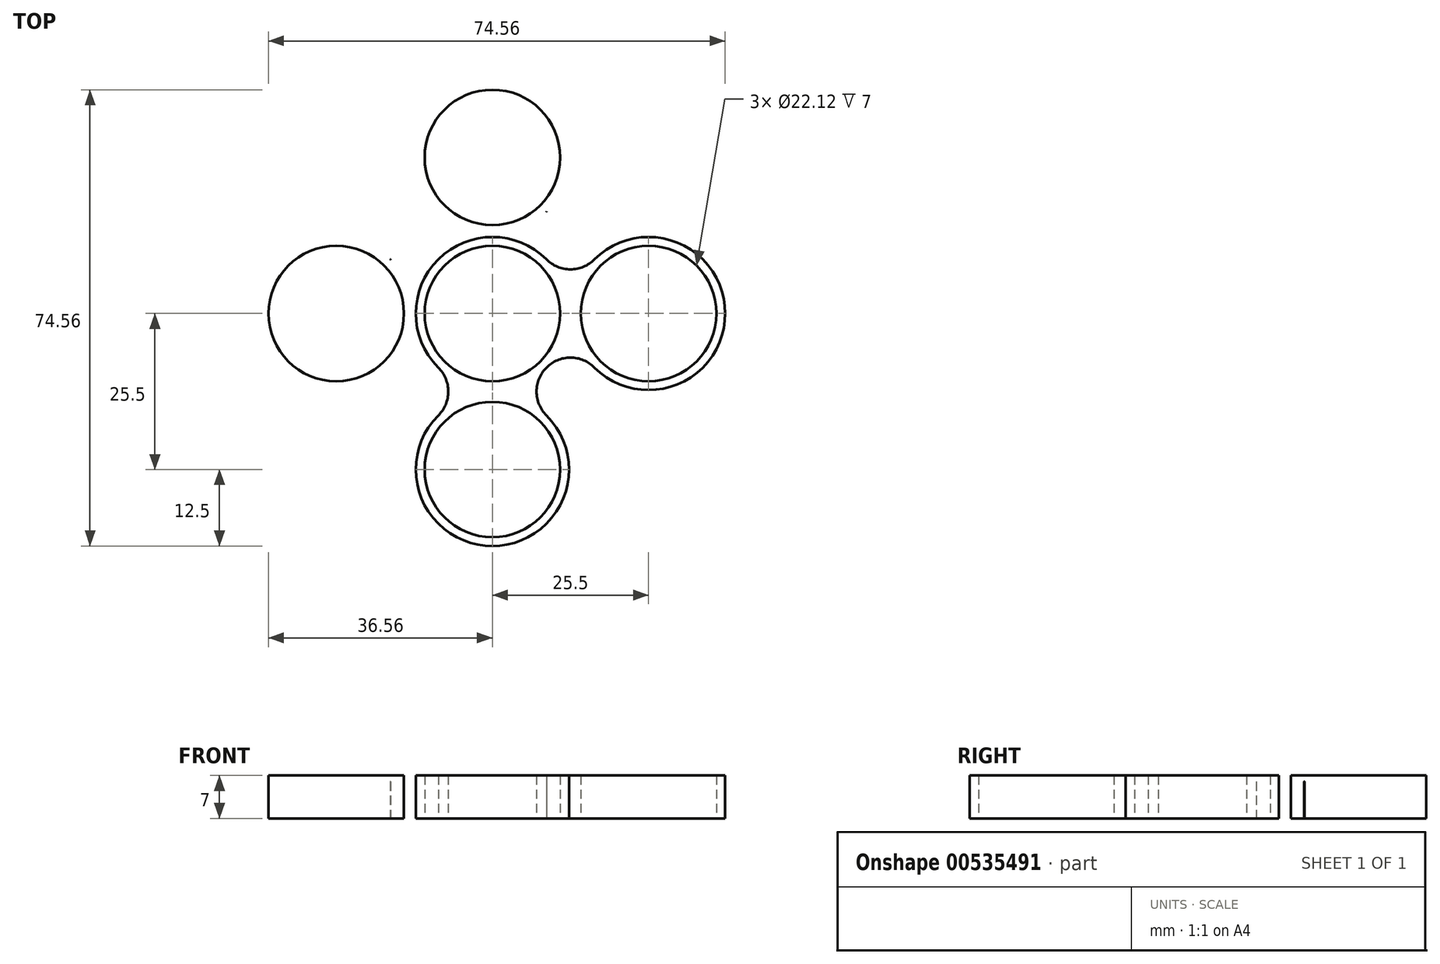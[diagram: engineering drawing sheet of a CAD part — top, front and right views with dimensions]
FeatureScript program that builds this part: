
annotation { "Feature Type Name" : "Feature", "Feature Type Description" : "" }
export const myFeature = defineFeature(function(context is Context, id is Id, definition is map)
    precondition{}
    {
        {
            var Q0;
            Q0=qCreatedBy(makeId("Top.planeOp"),FACE);
            var sketch = newSketch(context, id + "F0", { "sketchPlane" : qUnion([Q0])});
            skCircle(sketch, "E0", {"center": v(0, 0) * mm, "radius": 11.06 * mm});
            skCircle(sketch, "E1", {"center": v(0, 0) * mm, "radius": 12.5 * mm});
            skLineSegment(sketch, "E2", {"start": v(0, 0) * mm, "end": v(11.05, 11.05) * mm, "construction": true});
            skLineSegment(sketch, "E3", {"start": v(11.06, 0) * mm, "end": v(12.5, 0) * mm, "construction": true});
            skLineSegment(sketch, "E4", {"start": v(12.5, 0) * mm, "end": v(25.5, 0) * mm, "construction": true});
            skCircle(sketch, "E5", {"center": v(25.5, 0) * mm, "radius": 11.06 * mm});
            skCircle(sketch, "E6", {"center": v(25.5, 0) * mm, "radius": 12.5 * mm});
            skArc(sketch, "E7", {"start": v(8.84, 8.84) * mm, "mid": v(12.75, 7.2) * mm, "end": v(16.66, 8.84) * mm});
            skArc(sketch, "E8.MirrorCS", {"start": v(8.84, -8.84) * mm, "mid": v(12.75, -7.2) * mm, "end": v(16.66, -8.84) * mm});
            skCircle(sketch, "E9.MirrorC", {"center": v(0, 25.5) * mm, "radius": 12.5 * mm});
            skCircle(sketch, "E10.MirrorC", {"center": v(0, 25.5) * mm, "radius": 11.06 * mm});
            skArc(sketch, "E11.MirrorCS", {"start": v(8.84, 8.84) * mm, "mid": v(7.2, 12.75) * mm, "end": v(8.84, 16.66) * mm});
            skArc(sketch, "E12.MirrorCS", {"start": v(-8.84, 8.84) * mm, "mid": v(-7.2, 12.75) * mm, "end": v(-8.84, 16.66) * mm});
            skCircle(sketch, "E13.MirrorC", {"center": v(-25.5, 0) * mm, "radius": 11.06 * mm});
            skCircle(sketch, "E14.MirrorC", {"center": v(-25.5, 0) * mm, "radius": 12.5 * mm});
            skArc(sketch, "E15.MirrorCS", {"start": v(-8.84, 8.84) * mm, "mid": v(-12.75, 7.2) * mm, "end": v(-16.66, 8.84) * mm});
            skArc(sketch, "E16.MirrorCS", {"start": v(-8.84, -8.84) * mm, "mid": v(-12.75, -7.2) * mm, "end": v(-16.66, -8.84) * mm});
            skCircle(sketch, "E17.MirrorC", {"center": v(0, -25.5) * mm, "radius": 12.5 * mm});
            skCircle(sketch, "E18.MirrorC", {"center": v(0, -25.5) * mm, "radius": 11.06 * mm});
            skArc(sketch, "E19.MirrorCS", {"start": v(8.84, -8.84) * mm, "mid": v(7.2, -12.75) * mm, "end": v(8.84, -16.66) * mm});
            skArc(sketch, "E20.MirrorCS", {"start": v(-8.84, -8.84) * mm, "mid": v(-7.2, -12.75) * mm, "end": v(-8.84, -16.66) * mm});
            skSolve(sketch);
        }
        {
            var Q0;
            Q0=makeQuery(id+"F0.imprint","IMPRINT",FACE,{"disambiguationData":[TD([[makeQuery(id+"F0.imprint","IMPRINT",EDGE,{"derivedFrom":sQuery(id+"F0.wireOp",EDGE,"E0")}),-1.0]])]});
            var Q1;
            {var subQ0=sQuery(id+"F0.wireOp",EDGE,"uPQ4puG7-UEyB-lj3g-LrHJ-iqQRtvX8gU40");Q1=makeQuery(id+"F0.imprint","IMPRINT",FACE,{"disambiguationData":[TD([[makeQuery(id+"F0.imprint","IMPRINT",EDGE,{"derivedFrom":subQ0}),-1.0]])]});}
            var Q2;
            {var subQ0=sQuery(id+"F0.wireOp",EDGE,"09f7ae70-37af-4967-ad5b-0058ab8db1040.MirrorCS");Q2=makeQuery(id+"F0.imprint","IMPRINT",FACE,{"disambiguationData":[TD([[makeQuery(id+"F0.imprint","IMPRINT",EDGE,{"derivedFrom":subQ0}),1.0]])]});}
            var Q3;
            Q3=makeQuery(id+"F0.imprint","IMPRINT",FACE,{"disambiguationData":[TD([[makeQuery(id+"F0.imprint","IMPRINT",EDGE,{"derivedFrom":sQuery(id+"F0.wireOp",EDGE,"MIKsI08s-PwHs-qc6J-BAKb-bbBWn8hbvVMQ")}),1.0]])]});
            var Q4;
            Q4=makeQuery(id+"F0.imprint","IMPRINT",FACE,{"disambiguationData":[TD([[makeQuery(id+"F0.imprint","IMPRINT",EDGE,{"derivedFrom":sQuery(id+"F0.wireOp",EDGE,"MIKsI08s-PwHs-qc6J-BAKb-bbBWn8hbvVMQ")}),-1.0]])]});
            var Q5;
            {var subQ0=sQuery(id+"F0.wireOp",EDGE,"butBKBYa-hvjT-XOIa-KBhH-1ktqhelA6FoJ");var subQ1=sQuery(id+"F0.wireOp",EDGE,"E1");var subQ2=makeQuery(id+"F0.imprint","INTERSECT",VERTEX,{"disambiguationData":[OD(0.0)],"derivedFrom":[subQ1,subQ0]});Q5=makeQuery(id+"F0.imprint","IMPRINT",FACE,{"disambiguationData":[TD([[makeQuery(id+"F0.imprint","IMPRINT",EDGE,{"disambiguationData":[TD([[subQ2,1.0]])],"derivedFrom":subQ1}),1.0]])]});}
            var Q6;
            Q6=makeQuery(id+"F0.imprint","IMPRINT",FACE,{"disambiguationData":[TD([[makeQuery(id+"F0.imprint","IMPRINT",EDGE,{"derivedFrom":sQuery(id+"F0.wireOp",EDGE,"ioFQfvYo-xZlu-Zo4V-6zG4-lo5VrKWCEeY0")}),1.0]])]});
            var Q7;
            Q7=makeQuery(id+"F0.imprint","IMPRINT",FACE,{"disambiguationData":[TD([[makeQuery(id+"F0.imprint","IMPRINT",EDGE,{"derivedFrom":sQuery(id+"F0.wireOp",EDGE,"Zf5WaJAE-leRk-cjoL-8J3G-R3mTZz96XQRM")}),-1.0]])]});
            var Q8;
            {var subQ0=sQuery(id+"F0.wireOp",EDGE,"a43479c8-e354-4f77-97ad-e8487c43b59b0.MirrorCS");Q8=makeQuery(id+"F0.imprint","IMPRINT",FACE,{"disambiguationData":[TD([[makeQuery(id+"F0.imprint","IMPRINT",EDGE,{"derivedFrom":subQ0}),1.0]])]});}
            var Q9;
            Q9=makeQuery(id+"F0.imprint","IMPRINT",FACE,{"disambiguationData":[TD([[makeQuery(id+"F0.imprint","IMPRINT",EDGE,{"derivedFrom":sQuery(id+"F0.wireOp",EDGE,"ioFQfvYo-xZlu-Zo4V-6zG4-lo5VrKWCEeY0")}),-1.0]])]});
            var Q10;
            {var subQ0=sQuery(id+"F0.wireOp",EDGE,"kF5gWWsc-Utct-tbQF-3H6r-XP5KAdhgSgUx");Q10=makeQuery(id+"F0.imprint","IMPRINT",FACE,{"disambiguationData":[TD([[makeQuery(id+"F0.imprint","IMPRINT",EDGE,{"derivedFrom":subQ0}),-1.0]])]});}
            var Q11;
            {var subQ0=sQuery(id+"F0.wireOp",EDGE,"znM17040-PP66-ixoO-KGIn-lb9QrdvZVNfV");var subQ1=sQuery(id+"F0.wireOp",EDGE,"E1");var subQ2=makeQuery(id+"F0.imprint","INTERSECT",VERTEX,{"disambiguationData":[OD(0.0)],"derivedFrom":[subQ1,subQ0]});Q11=makeQuery(id+"F0.imprint","IMPRINT",FACE,{"disambiguationData":[TD([[makeQuery(id+"F0.imprint","IMPRINT",EDGE,{"disambiguationData":[TD([[subQ2,1.0]])],"derivedFrom":subQ1}),1.0]])]});}
            var Q12;
            Q12=makeQuery(id+"F0.imprint","IMPRINT",FACE,{"disambiguationData":[TD([[makeQuery(id+"F0.imprint","IMPRINT",EDGE,{"derivedFrom":sQuery(id+"F0.wireOp",EDGE,"E5")}),-1.0]])]});
            var Q13;
            {var subQ0=sQuery(id+"F0.wireOp",EDGE,"E7");Q13=makeQuery(id+"F0.imprint","IMPRINT",FACE,{"disambiguationData":[TD([[makeQuery(id+"F0.imprint","IMPRINT",EDGE,{"derivedFrom":subQ0}),-1.0]])]});}
            var Q14;
            Q14=makeQuery(id+"F0.imprint","IMPRINT",FACE,{"disambiguationData":[TD([[makeQuery(id+"F0.imprint","IMPRINT",EDGE,{"derivedFrom":sQuery(id+"F0.wireOp",EDGE,"E10.MirrorC")}),1.0]])]});
            var Q15;
            Q15=makeQuery(id+"F0.imprint","IMPRINT",FACE,{"disambiguationData":[TD([[makeQuery(id+"F0.imprint","IMPRINT",EDGE,{"derivedFrom":sQuery(id+"F0.wireOp",EDGE,"E13.MirrorC")}),1.0]])]});
            var Q16;
            Q16=makeQuery(id+"F0.imprint","IMPRINT",FACE,{"disambiguationData":[TD([[makeQuery(id+"F0.imprint","IMPRINT",EDGE,{"derivedFrom":sQuery(id+"F0.wireOp",EDGE,"E18.MirrorC")}),-1.0]])]});
            var Q17;
            {var subQ0=sQuery(id+"F0.wireOp",EDGE,"E11.MirrorCS");Q17=makeQuery(id+"F0.imprint","IMPRINT",FACE,{"disambiguationData":[TD([[makeQuery(id+"F0.imprint","IMPRINT",EDGE,{"derivedFrom":subQ0}),1.0]])]});}
            var Q18;
            {var subQ0=sQuery(id+"F0.wireOp",EDGE,"E15.MirrorCS");Q18=makeQuery(id+"F0.imprint","IMPRINT",FACE,{"disambiguationData":[TD([[makeQuery(id+"F0.imprint","IMPRINT",EDGE,{"derivedFrom":subQ0}),1.0]])]});}
            var Q19;
            {var subQ0=sQuery(id+"F0.wireOp",EDGE,"E19.MirrorCS");Q19=makeQuery(id+"F0.imprint","IMPRINT",FACE,{"disambiguationData":[TD([[makeQuery(id+"F0.imprint","IMPRINT",EDGE,{"derivedFrom":subQ0}),-1.0]])]});}
            extrude(context, id + "F1", {"entities" : qUnion([Q0, Q1, Q2, Q3, Q4, Q5, Q6, Q7, Q8, Q9, Q10, Q11, Q12, Q13, Q14, Q15, Q16, Q17, Q18, Q19]), "depth" : 7 * mm, "offsetDistance" : 25 * mm});
        }
        {
            var Q0;
            Q0=makeQuery(id+"F1.opExtrude","CAP_EDGE",EDGE,{"disambiguationData":[OSD([sQuery(id+"F0.wireOp",EDGE,"E0")])],"isStart":false});
            var Q1;
            Q1=makeQuery(id+"F1.opExtrude","CAP_EDGE",EDGE,{"disambiguationData":[OSD([sQuery(id+"F0.wireOp",EDGE,"E6")])],"isStart":true});
            var Q2;
            {var subQ0=sQuery(id+"F0.wireOp",EDGE,"E1");Q2=makeQuery(id+"F1.opExtrude","CAP_EDGE",EDGE,{"disambiguationData":[OSD([subQ0]),TDD([makeQuery(id+"F0.imprint","IMPRINT",EDGE,{"disambiguationData":[TD([[makeQuery(id+"F0.imprint","INTERSECT",VERTEX,{"derivedFrom":[subQ0,sQuery(id+"F0.wireOp",EDGE,"E7")]}),-1.0]])],"derivedFrom":subQ0})])],"isStart":true});}
            var Q3;
            {var subQ0=sQuery(id+"F0.wireOp",EDGE,"E1");Q3=makeQuery(id+"F1.opExtrude","CAP_EDGE",EDGE,{"disambiguationData":[OSD([subQ0]),TDD([makeQuery(id+"F0.imprint","IMPRINT",EDGE,{"disambiguationData":[TD([[makeQuery(id+"F0.imprint","INTERSECT",VERTEX,{"derivedFrom":[subQ0,sQuery(id+"F0.wireOp",EDGE,"E12.MirrorCS")]}),-1.0]])],"derivedFrom":subQ0})])],"isStart":true});}
            var Q4;
            {var subQ0=sQuery(id+"F0.wireOp",EDGE,"E1");Q4=makeQuery(id+"F1.opExtrude","CAP_EDGE",EDGE,{"disambiguationData":[OSD([subQ0]),TDD([makeQuery(id+"F0.imprint","IMPRINT",EDGE,{"disambiguationData":[TD([[makeQuery(id+"F0.imprint","INTERSECT",VERTEX,{"derivedFrom":[subQ0,sQuery(id+"F0.wireOp",EDGE,"E16.MirrorCS")]}),-1.0]])],"derivedFrom":subQ0})])],"isStart":true});}
            var Q5;
            {var subQ0=sQuery(id+"F0.wireOp",EDGE,"E1");Q5=makeQuery(id+"F1.opExtrude","CAP_EDGE",EDGE,{"disambiguationData":[OSD([subQ0]),TDD([makeQuery(id+"F0.imprint","IMPRINT",EDGE,{"disambiguationData":[TD([[makeQuery(id+"F0.imprint","INTERSECT",VERTEX,{"derivedFrom":[subQ0,sQuery(id+"F0.wireOp",EDGE,"E8.MirrorCS")]}),1.0]])],"derivedFrom":subQ0})])],"isStart":true});}
            var Q6;
            Q6=makeQuery(id+"F1.opExtrude","CAP_EDGE",EDGE,{"disambiguationData":[OSD([sQuery(id+"F0.wireOp",EDGE,"E8.MirrorCS")])],"isStart":false});
            var Q7;
            Q7=makeQuery(id+"F1.opExtrude","CAP_EDGE",EDGE,{"disambiguationData":[OSD([sQuery(id+"F0.wireOp",EDGE,"E6")])],"isStart":false});
            var Q8;
            Q8=makeQuery(id+"F1.opExtrude","CAP_EDGE",EDGE,{"disambiguationData":[OSD([sQuery(id+"F0.wireOp",EDGE,"E7")])],"isStart":false});
            var Q9;
            {var subQ0=sQuery(id+"F0.wireOp",EDGE,"E1");Q9=makeQuery(id+"F1.opExtrude","CAP_EDGE",EDGE,{"disambiguationData":[OSD([subQ0]),TDD([makeQuery(id+"F0.imprint","IMPRINT",EDGE,{"disambiguationData":[TD([[makeQuery(id+"F0.imprint","INTERSECT",VERTEX,{"derivedFrom":[subQ0,sQuery(id+"F0.wireOp",EDGE,"E7")]}),-1.0]])],"derivedFrom":subQ0})])],"isStart":false});}
            var Q10;
            {var subQ0=sQuery(id+"F0.wireOp",EDGE,"E1");Q10=makeQuery(id+"F1.opExtrude","CAP_EDGE",EDGE,{"disambiguationData":[OSD([subQ0]),TDD([makeQuery(id+"F0.imprint","IMPRINT",EDGE,{"disambiguationData":[TD([[makeQuery(id+"F0.imprint","INTERSECT",VERTEX,{"derivedFrom":[subQ0,sQuery(id+"F0.wireOp",EDGE,"E12.MirrorCS")]}),-1.0]])],"derivedFrom":subQ0})])],"isStart":false});}
            var Q11;
            {var subQ0=sQuery(id+"F0.wireOp",EDGE,"E1");Q11=makeQuery(id+"F1.opExtrude","CAP_EDGE",EDGE,{"disambiguationData":[OSD([subQ0]),TDD([makeQuery(id+"F0.imprint","IMPRINT",EDGE,{"disambiguationData":[TD([[makeQuery(id+"F0.imprint","INTERSECT",VERTEX,{"derivedFrom":[subQ0,sQuery(id+"F0.wireOp",EDGE,"E16.MirrorCS")]}),-1.0]])],"derivedFrom":subQ0})])],"isStart":false});}
            var Q12;
            {var subQ0=sQuery(id+"F0.wireOp",EDGE,"E1");Q12=makeQuery(id+"F1.opExtrude","CAP_EDGE",EDGE,{"disambiguationData":[OSD([subQ0]),TDD([makeQuery(id+"F0.imprint","IMPRINT",EDGE,{"disambiguationData":[TD([[makeQuery(id+"F0.imprint","INTERSECT",VERTEX,{"derivedFrom":[subQ0,sQuery(id+"F0.wireOp",EDGE,"E8.MirrorCS")]}),1.0]])],"derivedFrom":subQ0})])],"isStart":false});}
            var Q13;
            Q13=makeQuery(id+"F1.opExtrude","CAP_EDGE",EDGE,{"disambiguationData":[OSD([sQuery(id+"F0.wireOp",EDGE,"E14.MirrorC")])],"isStart":false});
            var Q14;
            Q14=makeQuery(id+"F1.opExtrude","CAP_EDGE",EDGE,{"disambiguationData":[OSD([sQuery(id+"F0.wireOp",EDGE,"E17.MirrorC")])],"isStart":false});
            var Q15;
            Q15=makeQuery(id+"F1.opExtrude","CAP_EDGE",EDGE,{"disambiguationData":[OSD([sQuery(id+"F0.wireOp",EDGE,"E9.MirrorC")])],"isStart":false});
            var Q16;
            Q16=makeQuery(id+"F1.opExtrude","CAP_EDGE",EDGE,{"disambiguationData":[OSD([sQuery(id+"F0.wireOp",EDGE,"E17.MirrorC")])],"isStart":true});
            var Q17;
            Q17=makeQuery(id+"F1.opExtrude","CAP_FACE",FACE,{"disambiguationData":[OSD([sQuery(id+"F0.wireOp",EDGE,"E0"),sQuery(id+"F0.wireOp",EDGE,"E1"),sQuery(id+"F0.wireOp",EDGE,"E5"),sQuery(id+"F0.wireOp",EDGE,"E6"),sQuery(id+"F0.wireOp",EDGE,"E7"),sQuery(id+"F0.wireOp",EDGE,"E8.MirrorCS"),sQuery(id+"F0.wireOp",EDGE,"E9.MirrorC"),sQuery(id+"F0.wireOp",EDGE,"E10.MirrorC"),sQuery(id+"F0.wireOp",EDGE,"E11.MirrorCS"),sQuery(id+"F0.wireOp",EDGE,"E12.MirrorCS"),sQuery(id+"F0.wireOp",EDGE,"E13.MirrorC"),sQuery(id+"F0.wireOp",EDGE,"E14.MirrorC"),sQuery(id+"F0.wireOp",EDGE,"E15.MirrorCS"),sQuery(id+"F0.wireOp",EDGE,"E16.MirrorCS"),sQuery(id+"F0.wireOp",EDGE,"E17.MirrorC"),sQuery(id+"F0.wireOp",EDGE,"E18.MirrorC"),sQuery(id+"F0.wireOp",EDGE,"E19.MirrorCS"),sQuery(id+"F0.wireOp",EDGE,"E20.MirrorCS")])],"isStart":true});
            fillet(context, id + "F2", {"entities" : qUnion([Q0, Q1, Q2, Q3, Q4, Q5, Q6, Q7, Q8, Q9, Q10, Q11, Q12, Q13, Q14, Q15, Q16, Q17]), "radius" : 1 * mm, "tangentPropagation" : true, "allowEdgeOverflow" : false});
        }
    });
